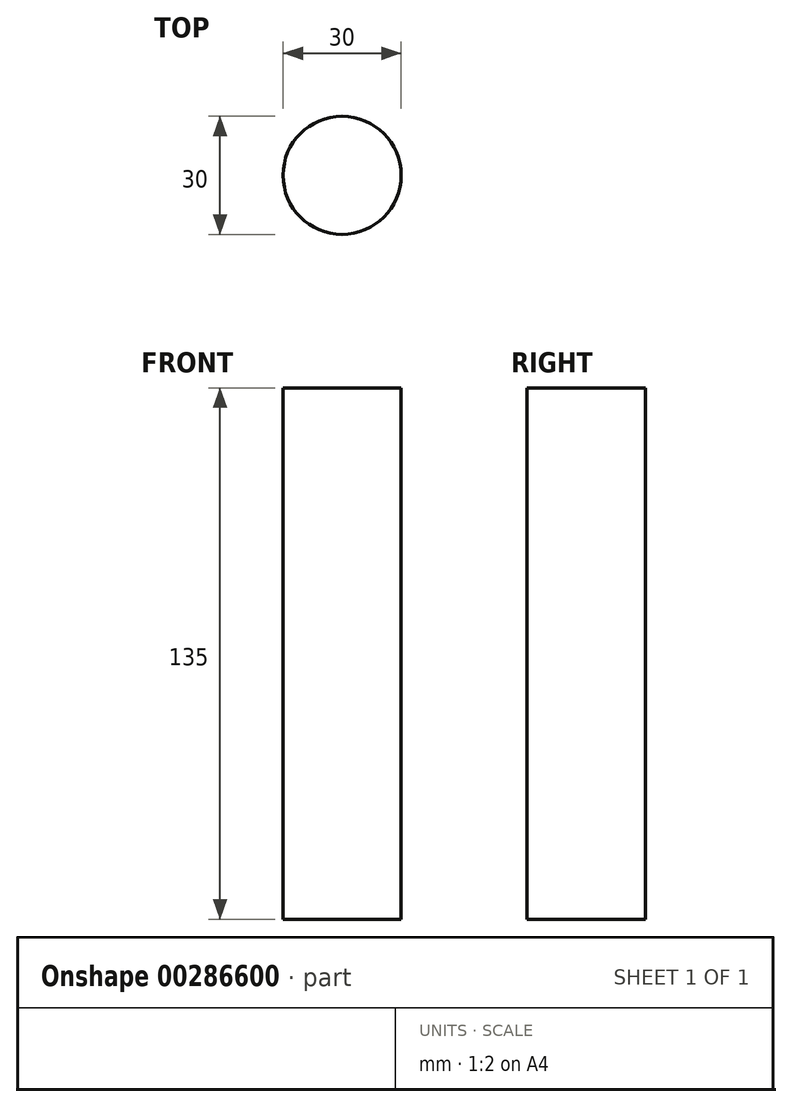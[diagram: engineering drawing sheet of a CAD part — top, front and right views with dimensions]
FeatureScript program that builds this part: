
annotation { "Feature Type Name" : "Feature", "Feature Type Description" : "" }
export const myFeature = defineFeature(function(context is Context, id is Id, definition is map)
    precondition{}
    {
        {
            var Q0;
            Q0=qCreatedBy(makeId("Top.planeOp"),FACE);
            var sketch = newSketch(context, id + "F0", { "sketchPlane" : qUnion([Q0])});
            skCircle(sketch, "E0", {"center": v(0, 0) * mm, "radius": 15 * mm});
            skSolve(sketch);
        }
        {
            var Q0;
            Q0=makeQuery(id+"F0.imprint","IMPRINT",FACE,{"disambiguationData":[TD([[makeQuery(id+"F0.imprint","IMPRINT",EDGE,{"derivedFrom":sQuery(id+"F0.wireOp",EDGE,"E0")}),1.0]])]});
            extrude(context, id + "F1", {"entities" : qUnion([Q0]), "depth" : 135 * mm});
        }
    });
